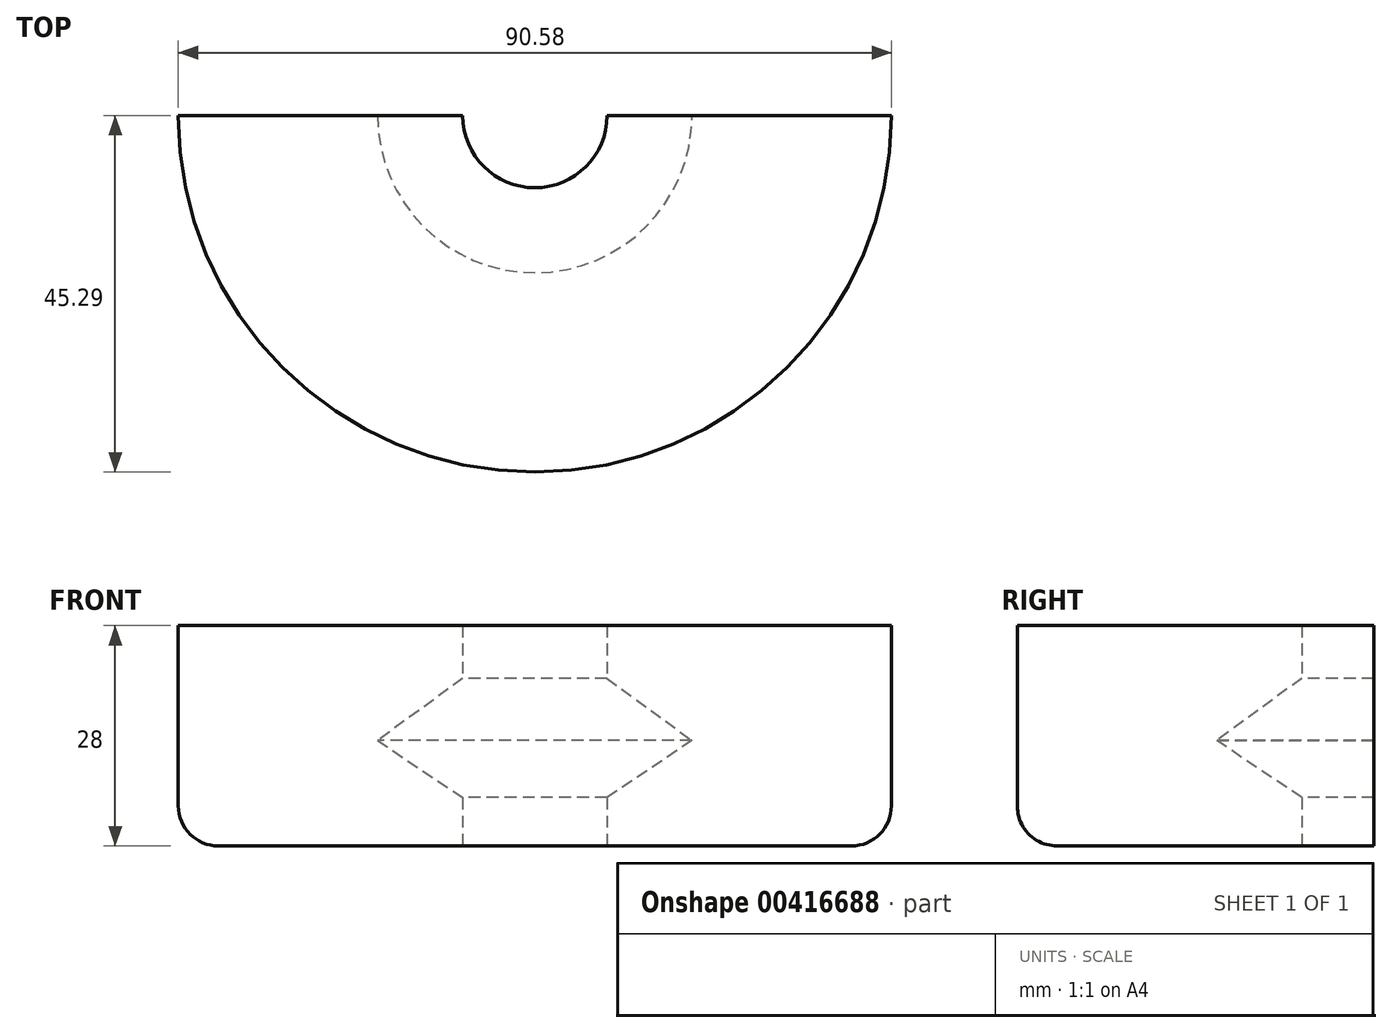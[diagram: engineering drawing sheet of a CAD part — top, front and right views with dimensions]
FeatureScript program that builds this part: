
annotation { "Feature Type Name" : "Feature", "Feature Type Description" : "" }
export const myFeature = defineFeature(function(context is Context, id is Id, definition is map)
    precondition{}
    {
        {
            var Q0;
            Q0=qCreatedBy(makeId("Front.planeOp"),FACE);
            var sketch = newSketch(context, id + "F0", { "sketchPlane" : qUnion([Q0])});
            skLineSegment(sketch, "E0.bottom", {"start": v(-9.17, 0) * mm, "end": v(-45.29, 0) * mm});
            skLineSegment(sketch, "E0.top", {"start": v(-9.17, 28) * mm, "end": v(-45.29, 28) * mm});
            skLineSegment(sketch, "E0.right", {"start": v(-45.29, 0) * mm, "end": v(-45.29, 28) * mm});
            skLineSegment(sketch, "E1", {"start": v(-9.17, 21.3) * mm, "end": v(-19.97, 13.4) * mm});
            skLineSegment(sketch, "E2", {"start": v(-19.97, 13.4) * mm, "end": v(-9.17, 6.15) * mm});
            skLineSegment(sketch, "E3", {"start": v(-9.17, 28) * mm, "end": v(-9.17, 21.3) * mm});
            skLineSegment(sketch, "E4.trimOffspring", {"start": v(-9.17, 6.15) * mm, "end": v(-9.17, 0) * mm});
            skLineSegment(sketch, "E5", {"start": v(0, 0) * mm, "end": v(0, 62.08) * mm, "construction": true});
            skSolve(sketch);
        }
        {
            var Q0;
            Q0=makeQuery(id+"F0.imprint","IMPRINT",FACE,{"disambiguationData":[TD([[makeQuery(id+"F0.imprint","IMPRINT",EDGE,{"derivedFrom":sQuery(id+"F0.wireOp",EDGE,"E0.bottom")}),-1.0]])]});
            var Q1;
            Q1=sQuery(id+"F0.wireOp",EDGE,"E5");
            revolve(context, id + "F1", {"entities" : qUnion([Q0]), "axis" : qUnion([Q1]), "revolveType" : RevolveType.ONE_DIRECTION, "angle" : 180 * degree});
        }
        {
            var Q0;
            Q0=makeQuery(id+"F1.opRevolve","SWEPT_EDGE",EDGE,{"disambiguationData":[OSD([sQuery(id+"F0.wireOp",EDGE,"E0.bottom"),sQuery(id+"F0.wireOp",EDGE,"E0.right")])]});
            fillet(context, id + "F2", {"entities" : qUnion([Q0]), "radius" : 5.08 * mm, "tangentPropagation" : true, "allowEdgeOverflow" : false});
        }
    });
